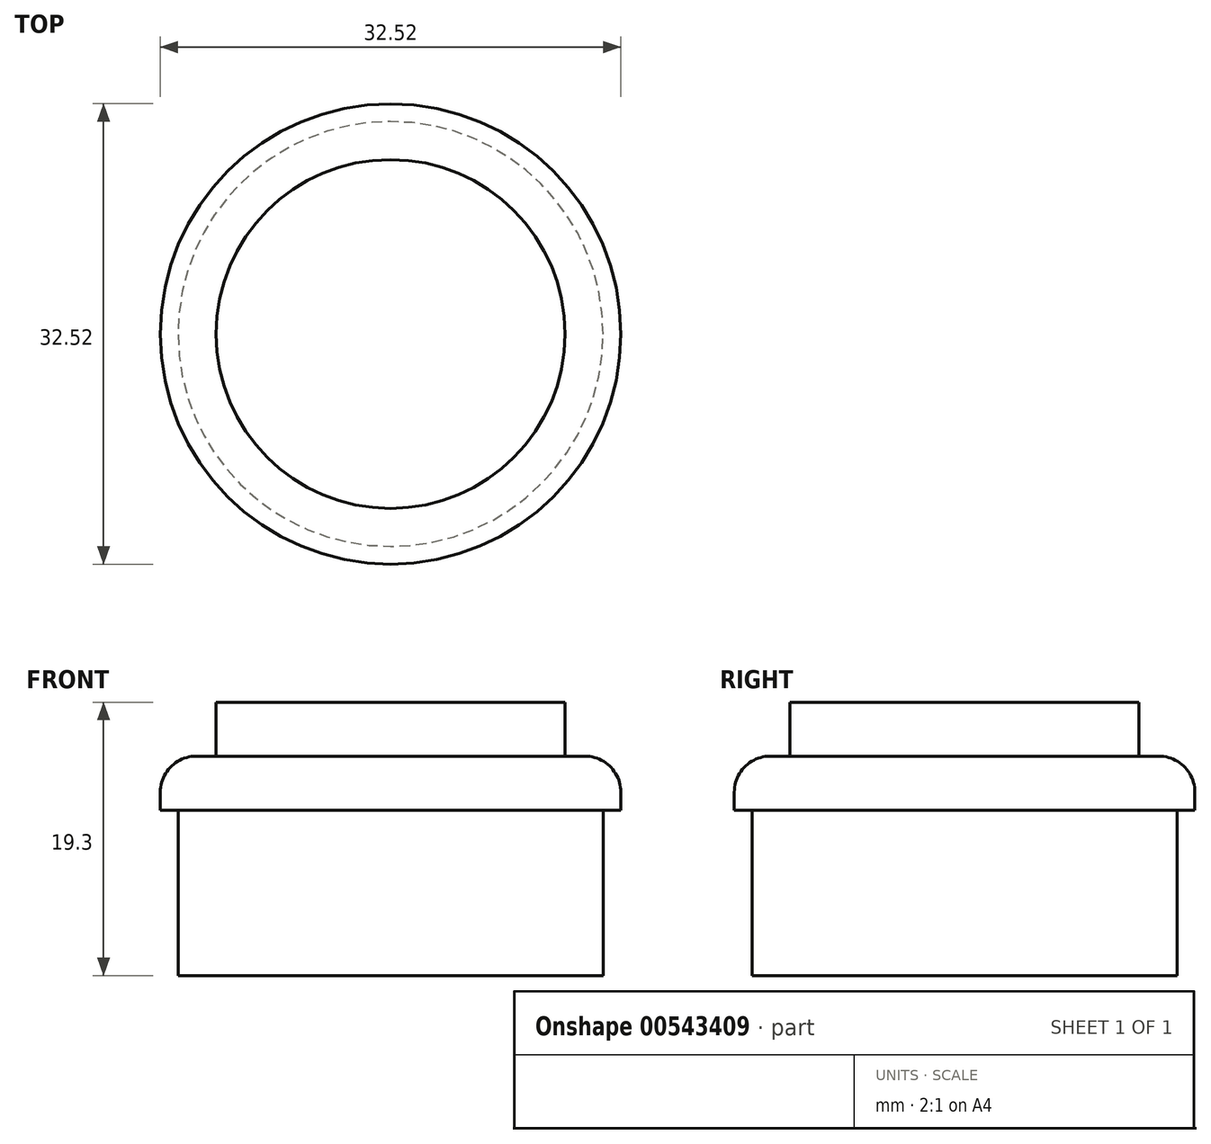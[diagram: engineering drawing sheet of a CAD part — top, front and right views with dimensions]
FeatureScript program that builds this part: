
annotation { "Feature Type Name" : "Feature", "Feature Type Description" : "" }
export const myFeature = defineFeature(function(context is Context, id is Id, definition is map)
    precondition{}
    {
        {
            var Q0;
            Q0=qCreatedBy(makeId("Front.planeOp"),FACE);
            var sketch = newSketch(context, id + "F0", { "sketchPlane" : qUnion([Q0])});
            skLineSegment(sketch, "E0", {"start": v(0, 7.62) * mm, "end": v(12.32, 7.62) * mm});
            skLineSegment(sketch, "E1", {"start": v(12.32, 7.62) * mm, "end": v(12.32, 3.8) * mm});
            skLineSegment(sketch, "E2", {"start": v(12.32, 3.8) * mm, "end": v(16.26, 3.8) * mm});
            skLineSegment(sketch, "E3", {"start": v(16.26, 3.8) * mm, "end": v(16.26, 0) * mm});
            skLineSegment(sketch, "E4", {"start": v(16.26, 0) * mm, "end": v(15, 0) * mm});
            skLineSegment(sketch, "E5", {"start": v(15, 0) * mm, "end": v(15, -11.68) * mm});
            skLineSegment(sketch, "E6", {"start": v(15, -11.68) * mm, "end": v(0, -11.68) * mm});
            skLineSegment(sketch, "E7", {"start": v(0, -11.68) * mm, "end": v(0, 7.62) * mm, "construction": true});
            skLineSegment(sketch, "E8", {"start": v(0, 7.62) * mm, "end": v(0, -11.68) * mm});
            skSolve(sketch);
        }
        {
            var Q0;
            Q0 = qSketchRegion(id + "F0", true);
            var Q1;
            Q1=sQuery(id+"F0.wireOp",EDGE,"E8");
            revolve(context, id + "F1", {"entities" : qUnion([Q0]), "axis" : qUnion([Q1]), "revolveType" : RevolveType.FULL});
        }
        {
            var Q0;
            Q0=makeQuery(id+"F1.opRevolve","SWEPT_EDGE",EDGE,{"disambiguationData":[OSD([sQuery(id+"F0.wireOp",EDGE,"E2"),sQuery(id+"F0.wireOp",EDGE,"E3")])]});
            fillet(context, id + "F2", {"entities" : qUnion([Q0]), "radius" : 2.54 * mm, "tangentPropagation" : true, "allowEdgeOverflow" : false});
        }
    });
